annotation { "Feature Type Name" : "Feature", "Feature Type Description" : "" }
export const myFeature = defineFeature(function(context is Context, id is Id, definition is map)
    precondition{}
    {
        {
            var Q0;
            Q0=qCreatedBy(makeId("Top.planeOp"),FACE);
            var sketch = newSketch(context, id + "F0", { "sketchPlane" : qUnion([Q0])});
            skLineSegment(sketch, "E0", {"start": v(0, 0) * mm, "end": v(10, 0) * mm});
            skLineSegment(sketch, "E1", {"start": v(10, 0) * mm, "end": v(10, -5) * mm});
            skLineSegment(sketch, "E2", {"start": v(10, -5) * mm, "end": v(35, -5) * mm});
            skLineSegment(sketch, "E3", {"start": v(35, -5) * mm, "end": v(35, 0) * mm});
            skLineSegment(sketch, "E4", {"start": v(35, 0) * mm, "end": v(153.3, 0) * mm});
            skLineSegment(sketch, "E5", {"start": v(153.3, 0) * mm, "end": v(153.3, -5) * mm});
            skLineSegment(sketch, "E6", {"start": v(153.3, -5) * mm, "end": v(178.3, -5) * mm});
            skLineSegment(sketch, "E7", {"start": v(178.3, -5) * mm, "end": v(178.3, 0) * mm});
            skLineSegment(sketch, "E8", {"start": v(178.3, 0) * mm, "end": v(188, 0) * mm});
            skLineSegment(sketch, "E9", {"start": v(0, 0) * mm, "end": v(0, 6.59) * mm});
            skLineSegment(sketch, "E10", {"start": v(3.18, 11.24) * mm, "end": v(128, 60) * mm});
            skLineSegment(sketch, "E11", {"start": v(128, 60) * mm, "end": v(148, 60) * mm});
            skLineSegment(sketch, "E12", {"start": v(188, 0) * mm, "end": v(188, 8.25) * mm});
            skLineSegment(sketch, "E13", {"start": v(186.9, 11.37) * mm, "end": v(148, 60) * mm});
            skPoint(sketch, "E14", {"position": v(138, 60) * mm});
            skPoint(sketch, "E15.visualSharp", {"position": v(0, 10) * mm});
            skArc(sketch, "E15.filletArc", {"start": v(3.18, 11.24) * mm, "mid": v(0.87, 9.4) * mm, "end": v(0, 6.59) * mm});
            skPoint(sketch, "E16.visualSharp", {"position": v(188, 10) * mm});
            skArc(sketch, "E16.filletArc", {"start": v(188, 8.25) * mm, "mid": v(187.72, 9.9) * mm, "end": v(186.9, 11.37) * mm});
            skLineSegment(sketch, "E17", {"start": v(172.86, 16.12) * mm, "end": v(145.66, 50.12) * mm});
            skLineSegment(sketch, "E18", {"start": v(141.75, 52) * mm, "end": v(130.45, 52) * mm});
            skLineSegment(sketch, "E19", {"start": v(128.63, 51.66) * mm, "end": v(41.59, 17.66) * mm});
            skLineSegment(sketch, "E20", {"start": v(43.4, 8) * mm, "end": v(168.95, 8) * mm});
            skPoint(sketch, "E21.orphan", {"position": v(5, 3.36) * mm});
            skPoint(sketch, "E22.visualSharp", {"position": v(16.87, 8) * mm});
            skArc(sketch, "E22.filletArc", {"start": v(41.59, 17.66) * mm, "mid": v(38.5, 12.07) * mm, "end": v(43.4, 8) * mm});
            skPoint(sketch, "E23.visualSharp", {"position": v(179.36, 8) * mm});
            skArc(sketch, "E23.filletArc", {"start": v(168.95, 8) * mm, "mid": v(173.46, 10.83) * mm, "end": v(172.86, 16.12) * mm});
            skPoint(sketch, "E24.visualSharp", {"position": v(144.16, 52) * mm});
            skArc(sketch, "E24.filletArc", {"start": v(145.66, 50.12) * mm, "mid": v(143.92, 51.5) * mm, "end": v(141.75, 52) * mm});
            skPoint(sketch, "E25.visualSharp", {"position": v(129.5, 52) * mm});
            skArc(sketch, "E25.filletArc", {"start": v(130.45, 52) * mm, "mid": v(129.52, 51.91) * mm, "end": v(128.63, 51.66) * mm});
            skText(sketch, "E26", { "text": "ECU FAB", "fontName": "OpenSans-Bold.ttf"});
            const initialGuessF0  = {"E26": [0.06902, 0.008, 1, 0, 0.01313]};
            skSetInitialGuess(sketch, initialGuessF0);
            skSolve(sketch);
        }
        {
            var Q0;
            {var subQ0=sQuery(id+"F0.wireOp",EDGE,"E26.sketch_text.stroke-31");var subQ1=sQuery(id+"F0.wireOp",EDGE,"E20");var subQ2=makeQuery(id+"F0.imprint","INTERSECT",VERTEX,{"derivedFrom":[subQ1,subQ0]});Q0=makeQuery(id+"F0.imprint","IMPRINT",FACE,{"disambiguationData":[TD([[makeQuery(id+"F0.imprint","IMPRINT",EDGE,{"disambiguationData":[TD([[subQ2,-1.0]])],"derivedFrom":subQ1}),-1.0]])]});}
            var Q1;
            Q1=makeQuery(id+"F0.imprint","IMPRINT",FACE,{"disambiguationData":[TD([[makeQuery(id+"F0.imprint","IMPRINT",EDGE,{"derivedFrom":sQuery(id+"F0.wireOp",EDGE,"E26.sketch_text.stroke-27")}),-1.0]])]});
            var Q2;
            {var subQ0=sQuery(id+"F0.wireOp",EDGE,"E26.sketch_text.stroke-18");var subQ1=sQuery(id+"F0.wireOp",EDGE,"E20");var subQ2=makeQuery(id+"F0.imprint","INTERSECT",VERTEX,{"derivedFrom":[subQ1,subQ0]});Q2=makeQuery(id+"F0.imprint","IMPRINT",FACE,{"disambiguationData":[TD([[makeQuery(id+"F0.imprint","IMPRINT",EDGE,{"disambiguationData":[TD([[subQ2,-1.0]])],"derivedFrom":subQ1}),-1.0]])]});}
            var Q3;
            Q3=makeQuery(id+"F0.imprint","IMPRINT",FACE,{"disambiguationData":[TD([[makeQuery(id+"F0.imprint","IMPRINT",EDGE,{"derivedFrom":sQuery(id+"F0.wireOp",EDGE,"E26.sketch_text.stroke-12")}),-1.0]])]});
            var Q4;
            Q4=makeQuery(id+"F0.imprint","IMPRINT",FACE,{"disambiguationData":[TD([[makeQuery(id+"F0.imprint","IMPRINT",EDGE,{"derivedFrom":sQuery(id+"F0.wireOp",EDGE,"E0")}),1.0]])]});
            var Q5;
            Q5=makeQuery(id+"F0.imprint","IMPRINT",FACE,{"disambiguationData":[TD([[makeQuery(id+"F0.imprint","IMPRINT",EDGE,{"derivedFrom":sQuery(id+"F0.wireOp",EDGE,"E26.sketch_text.stroke-42")}),-1.0]])]});
            var Q6;
            Q6=makeQuery(id+"F0.imprint","IMPRINT",FACE,{"disambiguationData":[TD([[makeQuery(id+"F0.imprint","IMPRINT",EDGE,{"derivedFrom":sQuery(id+"F0.wireOp",EDGE,"E26.sketch_text.stroke-52")}),-1.0]])]});
            var Q7;
            Q7=makeQuery(id+"F0.imprint","IMPRINT",FACE,{"disambiguationData":[TD([[makeQuery(id+"F0.imprint","IMPRINT",EDGE,{"derivedFrom":sQuery(id+"F0.wireOp",EDGE,"E26.sketch_text.stroke-64")}),-1.0]])]});
            var Q8;
            Q8=makeQuery(id+"F0.imprint","IMPRINT",FACE,{"disambiguationData":[TD([[makeQuery(id+"F0.imprint","IMPRINT",EDGE,{"derivedFrom":sQuery(id+"F0.wireOp",EDGE,"E26.sketch_text.stroke-0")}),-1.0]])]});
            extrude(context, id + "F1", {"entities" : qUnion([Q0, Q1, Q2, Q3, Q4, Q5, Q6, Q7, Q8]), "depth" : 5 * mm});
        }
    });